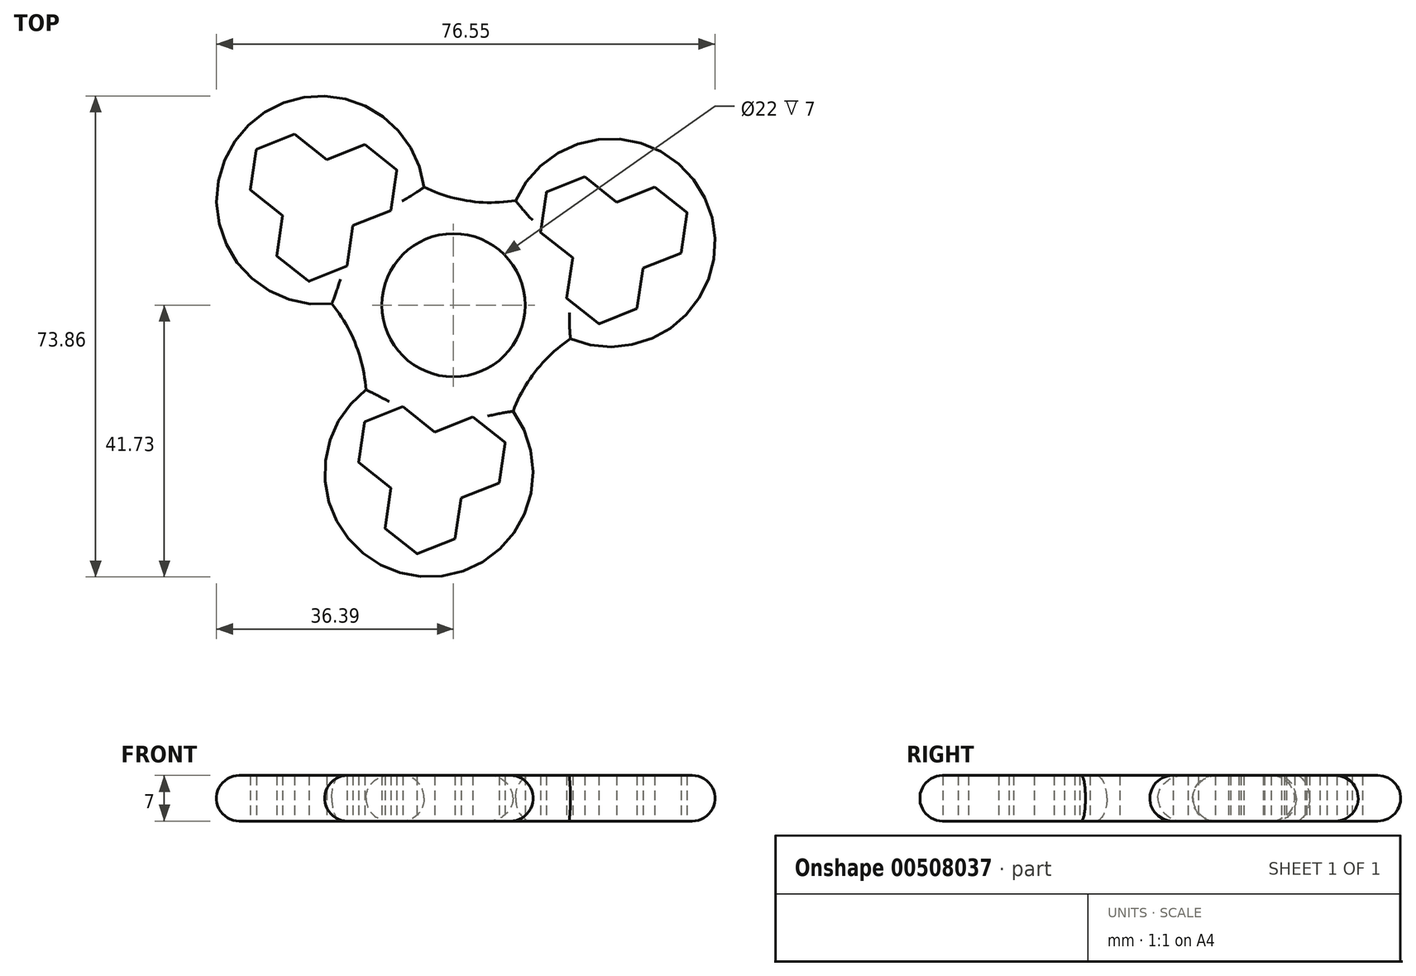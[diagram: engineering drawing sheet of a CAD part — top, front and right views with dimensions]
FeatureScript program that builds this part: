
annotation { "Feature Type Name" : "Feature", "Feature Type Description" : "" }
export const myFeature = defineFeature(function(context is Context, id is Id, definition is map)
    precondition{}
    {
        {
            var Q0;
            Q0=qCreatedBy(makeId("Top.planeOp"),FACE);
            var sketch = newSketch(context, id + "F0", { "sketchPlane" : qUnion([Q0])});
            skCircle(sketch, "E0", {"center": v(0, 0) * mm, "radius": 15 * mm});
            skCircle(sketch, "E1", {"center": v(0, 0) * mm, "radius": 11 * mm});
            skLineSegment(sketch, "E2", {"start": v(0, 0) * mm, "end": v(-20.4, 16.13) * mm});
            skLineSegment(sketch, "E3", {"start": v(0, 0) * mm, "end": v(24.16, 9.6) * mm});
            skLineSegment(sketch, "E4", {"start": v(0, 0) * mm, "end": v(-3.77, -25.73) * mm});
            skPoint(sketch, "E5.0.midPoint", {"position": v(-16.08, 12.72) * mm});
            skPoint(sketch, "E6.0.midPoint", {"position": v(19.05, 7.57) * mm});
            skPoint(sketch, "E7.0.midPoint", {"position": v(-2.97, -20.28) * mm});
            skCircle(sketch, "E8", {"center": v(-3.77, -25.73) * mm, "radius": 16 * mm});
            skCircle(sketch, "E9", {"center": v(-20.4, 16.13) * mm, "radius": 16 * mm});
            skCircle(sketch, "E10", {"center": v(24.16, 9.6) * mm, "radius": 16 * mm});
            skCircle(sketch, "E11.cCircle", {"center": v(-25.33, 20.03) * mm, "radius": 6.3 * mm, "construction": true});
            skLineSegment(sketch, "E11.0", {"start": v(-19.48, 22.35) * mm, "end": v(-20.4, 16.13) * mm});
            skLineSegment(sketch, "E11.1", {"start": v(-20.4, 16.13) * mm, "end": v(-26.24, 13.8) * mm});
            skLineSegment(sketch, "E11.2", {"start": v(-26.24, 13.8) * mm, "end": v(-31.18, 17.7) * mm});
            skLineSegment(sketch, "E11.3", {"start": v(-31.18, 17.7) * mm, "end": v(-30.27, 23.93) * mm});
            skLineSegment(sketch, "E11.4", {"start": v(-30.27, 23.93) * mm, "end": v(-24.42, 26.26) * mm});
            skLineSegment(sketch, "E11.5", {"start": v(-24.42, 26.26) * mm, "end": v(-19.48, 22.35) * mm});
            skCircle(sketch, "E12.cCircle", {"center": v(-14.55, 18.45) * mm, "radius": 6.3 * mm, "construction": true});
            skLineSegment(sketch, "E12.0", {"start": v(-8.7, 20.77) * mm, "end": v(-9.6, 14.55) * mm});
            skLineSegment(sketch, "E12.1", {"start": v(-9.6, 14.55) * mm, "end": v(-15.46, 12.22) * mm});
            skLineSegment(sketch, "E12.2", {"start": v(-15.46, 12.22) * mm, "end": v(-20.4, 16.13) * mm});
            skLineSegment(sketch, "E12.3", {"start": v(-20.4, 16.13) * mm, "end": v(-19.48, 22.35) * mm});
            skLineSegment(sketch, "E12.4", {"start": v(-19.48, 22.35) * mm, "end": v(-13.63, 24.68) * mm});
            skLineSegment(sketch, "E12.5", {"start": v(-13.63, 24.68) * mm, "end": v(-8.7, 20.77) * mm});
            skCircle(sketch, "E13.cCircle", {"center": v(-21.3, 9.9) * mm, "radius": 6.3 * mm, "construction": true});
            skLineSegment(sketch, "E13.0", {"start": v(-16.37, 6) * mm, "end": v(-22.22, 3.67) * mm});
            skLineSegment(sketch, "E13.1", {"start": v(-22.22, 3.67) * mm, "end": v(-27.16, 7.58) * mm});
            skLineSegment(sketch, "E13.2", {"start": v(-27.16, 7.58) * mm, "end": v(-26.24, 13.8) * mm});
            skLineSegment(sketch, "E13.3", {"start": v(-26.24, 13.8) * mm, "end": v(-20.4, 16.13) * mm});
            skLineSegment(sketch, "E13.4", {"start": v(-20.4, 16.13) * mm, "end": v(-15.46, 12.22) * mm});
            skLineSegment(sketch, "E13.5", {"start": v(-15.46, 12.22) * mm, "end": v(-16.37, 6) * mm});
            skCircle(sketch, "E14.MirrorC", {"center": v(30.01, 11.92) * mm, "radius": 6.3 * mm, "construction": true});
            skCircle(sketch, "E15.MirrorC", {"center": v(19.23, 13.5) * mm, "radius": 6.3 * mm, "construction": true});
            skCircle(sketch, "E16.MirrorC", {"center": v(23.25, 3.37) * mm, "radius": 6.3 * mm, "construction": true});
            skLineSegment(sketch, "E17.MirrorCS", {"start": v(30.92, 18.15) * mm, "end": v(25.08, 15.82) * mm});
            skLineSegment(sketch, "E18.MirrorCS", {"start": v(35.86, 14.24) * mm, "end": v(30.92, 18.15) * mm});
            skLineSegment(sketch, "E19.MirrorCS", {"start": v(34.95, 8.02) * mm, "end": v(35.86, 14.24) * mm});
            skLineSegment(sketch, "E20.MirrorCS", {"start": v(29.1, 5.7) * mm, "end": v(34.95, 8.02) * mm});
            skLineSegment(sketch, "E21.MirrorCS", {"start": v(24.16, 9.6) * mm, "end": v(29.1, 5.7) * mm});
            skLineSegment(sketch, "E22.MirrorCS", {"start": v(25.08, 15.82) * mm, "end": v(24.16, 9.6) * mm});
            skLineSegment(sketch, "E23.MirrorCS", {"start": v(25.08, 15.82) * mm, "end": v(20.14, 19.73) * mm});
            skLineSegment(sketch, "E24.MirrorCS", {"start": v(20.14, 19.73) * mm, "end": v(14.3, 17.4) * mm});
            skLineSegment(sketch, "E25.MirrorCS", {"start": v(14.3, 17.4) * mm, "end": v(13.38, 11.18) * mm});
            skLineSegment(sketch, "E26.MirrorCS", {"start": v(13.38, 11.18) * mm, "end": v(18.31, 7.28) * mm});
            skLineSegment(sketch, "E27.MirrorCS", {"start": v(18.31, 7.28) * mm, "end": v(24.16, 9.6) * mm});
            skLineSegment(sketch, "E28.MirrorCS", {"start": v(28.19, -0.53) * mm, "end": v(29.1, 5.7) * mm});
            skLineSegment(sketch, "E29.MirrorCS", {"start": v(22.34, -2.85) * mm, "end": v(28.19, -0.53) * mm});
            skLineSegment(sketch, "E30.MirrorCS", {"start": v(17.4, 1.05) * mm, "end": v(22.34, -2.85) * mm});
            skLineSegment(sketch, "E31.MirrorCS", {"start": v(18.31, 7.28) * mm, "end": v(17.4, 1.05) * mm});
            skLineSegment(sketch, "E32.MirrorCS", {"start": v(-14.55, -24.15) * mm, "end": v(-13.64, -17.92) * mm});
            skLineSegment(sketch, "E33.MirrorCS", {"start": v(-9.62, -28.05) * mm, "end": v(-14.55, -24.15) * mm});
            skLineSegment(sketch, "E34.MirrorCS", {"start": v(-13.64, -17.92) * mm, "end": v(-7.8, -15.6) * mm});
            skLineSegment(sketch, "E35.MirrorCS", {"start": v(-9.62, -28.05) * mm, "end": v(-3.77, -25.73) * mm});
            skLineSegment(sketch, "E36.MirrorCS", {"start": v(-10.53, -34.28) * mm, "end": v(-9.62, -28.05) * mm});
            skLineSegment(sketch, "E37.MirrorCS", {"start": v(-5.6, -38.18) * mm, "end": v(-10.53, -34.28) * mm});
            skLineSegment(sketch, "E38.MirrorCS", {"start": v(0.25, -35.86) * mm, "end": v(-5.6, -38.18) * mm});
            skLineSegment(sketch, "E39.MirrorCS", {"start": v(1.17, -29.63) * mm, "end": v(0.25, -35.86) * mm});
            skLineSegment(sketch, "E40.MirrorCS", {"start": v(-3.77, -25.73) * mm, "end": v(1.17, -29.63) * mm});
            skLineSegment(sketch, "E41.MirrorCS", {"start": v(-2.86, -19.5) * mm, "end": v(3, -17.18) * mm});
            skLineSegment(sketch, "E42.MirrorCS", {"start": v(7.02, -27.3) * mm, "end": v(1.17, -29.63) * mm});
            skLineSegment(sketch, "E43.MirrorCS", {"start": v(7.93, -21.08) * mm, "end": v(7.02, -27.3) * mm});
            skLineSegment(sketch, "E44.MirrorCS", {"start": v(3, -17.18) * mm, "end": v(7.93, -21.08) * mm});
            skLineSegment(sketch, "E45.MirrorCS", {"start": v(-7.8, -15.6) * mm, "end": v(-2.86, -19.5) * mm});
            skCircle(sketch, "E46.MirrorC", {"center": v(-8.7, -21.82) * mm, "radius": 6.3 * mm, "construction": true});
            skCircle(sketch, "E47.MirrorC", {"center": v(-4.68, -31.95) * mm, "radius": 6.3 * mm, "construction": true});
            skCircle(sketch, "E48.MirrorC", {"center": v(2.08, -23.4) * mm, "radius": 6.3 * mm, "construction": true});
            skLineSegment(sketch, "E49", {"start": v(-8.7, 20.77) * mm, "end": v(14.3, 17.4) * mm, "construction": true});
            skLineSegment(sketch, "E50", {"start": v(22.34, -2.85) * mm, "end": v(7.93, -21.08) * mm, "construction": true});
            skLineSegment(sketch, "E51", {"start": v(-13.64, -17.92) * mm, "end": v(-22.22, 3.67) * mm, "construction": true});
            skArc(sketch, "E52", {"start": v(-8.7, 20.77) * mm, "mid": v(2.35, 16) * mm, "end": v(14.3, 17.4) * mm});
            skArc(sketch, "E53", {"start": v(22.34, -2.85) * mm, "mid": v(12.7, -10.04) * mm, "end": v(7.93, -21.08) * mm});
            skArc(sketch, "E54", {"start": v(-13.64, -17.92) * mm, "mid": v(-15.04, -5.97) * mm, "end": v(-22.22, 3.67) * mm});
            skSolve(sketch);
        }
        {
            var Q0;
            Q0=qSketchRegion(id+"F0",true);
            var Q1;
            {var subQ5=sQuery(id+"F0.wireOp",EDGE,"E10");var subQ6=sQuery(id+"F0.wireOp",EDGE,"E0");var subQ7=makeQuery(id+"F0.imprint","INTERSECT",VERTEX,{"disambiguationData":[OD(1.0)],"derivedFrom":[subQ6,subQ5]});Q1=makeQuery(id+"F0.imprint","IMPRINT",FACE,{"disambiguationData":[TD([[makeQuery(id+"F0.imprint","IMPRINT",EDGE,{"disambiguationData":[TD([[subQ7,-1.0]])],"derivedFrom":subQ6}),1.0]])]});}
            var Q2;
            {var subQ3=sQuery(id+"F0.wireOp",EDGE,"E10");var subQ6=sQuery(id+"F0.wireOp",EDGE,"E0");var subQ10=makeQuery(id+"F0.imprint","INTERSECT",VERTEX,{"disambiguationData":[OD(0.0)],"derivedFrom":[subQ6,subQ3]});Q2=makeQuery(id+"F0.imprint","IMPRINT",FACE,{"disambiguationData":[TD([[makeQuery(id+"F0.imprint","IMPRINT",EDGE,{"disambiguationData":[TD([[subQ10,1.0]])],"derivedFrom":subQ6}),1.0]])]});}
            var Q3;
            {var subQ1=sQuery(id+"F0.wireOp",EDGE,"E0");var subQ8=sQuery(id+"F0.wireOp",EDGE,"E9");var subQ11=makeQuery(id+"F0.imprint","INTERSECT",VERTEX,{"disambiguationData":[OD(1.0)],"derivedFrom":[subQ1,subQ8]});Q3=makeQuery(id+"F0.imprint","IMPRINT",FACE,{"disambiguationData":[TD([[makeQuery(id+"F0.imprint","IMPRINT",EDGE,{"disambiguationData":[TD([[subQ11,-1.0]])],"derivedFrom":subQ1}),1.0]])]});}
            var Q4;
            {var subQ0=sQuery(id+"F0.wireOp",EDGE,"E2");var subQ1=sQuery(id+"F0.wireOp",EDGE,"E0");var subQ2=makeQuery(id+"F0.imprint","INTERSECT",VERTEX,{"derivedFrom":[subQ1,subQ0]});Q4=makeQuery(id+"F0.imprint","IMPRINT",FACE,{"disambiguationData":[TD([[makeQuery(id+"F0.imprint","IMPRINT",EDGE,{"disambiguationData":[TD([[subQ2,-1.0]])],"derivedFrom":subQ1}),1.0]])]});}
            var Q5;
            {var subQ0=sQuery(id+"F0.wireOp",EDGE,"E9");var subQ1=sQuery(id+"F0.wireOp",EDGE,"E0");var subQ2=makeQuery(id+"F0.imprint","INTERSECT",VERTEX,{"disambiguationData":[OD(0.0)],"derivedFrom":[subQ1,subQ0]});Q5=makeQuery(id+"F0.imprint","IMPRINT",FACE,{"disambiguationData":[TD([[makeQuery(id+"F0.imprint","IMPRINT",EDGE,{"disambiguationData":[TD([[subQ2,-1.0]])],"derivedFrom":subQ1}),1.0]])]});}
            var Q6;
            {var subQ0=sQuery(id+"F0.wireOp",EDGE,"E3");var subQ1=sQuery(id+"F0.wireOp",EDGE,"E0");var subQ2=makeQuery(id+"F0.imprint","INTERSECT",VERTEX,{"derivedFrom":[subQ1,subQ0]});Q6=makeQuery(id+"F0.imprint","IMPRINT",FACE,{"disambiguationData":[TD([[makeQuery(id+"F0.imprint","IMPRINT",EDGE,{"disambiguationData":[TD([[subQ2,-1.0]])],"derivedFrom":subQ1}),1.0]])]});}
            var Q7;
            {var subQ0=sQuery(id+"F0.wireOp",EDGE,"E3");var subQ1=sQuery(id+"F0.wireOp",EDGE,"E0");var subQ2=makeQuery(id+"F0.imprint","INTERSECT",VERTEX,{"derivedFrom":[subQ1,subQ0]});Q7=makeQuery(id+"F0.imprint","IMPRINT",FACE,{"disambiguationData":[TD([[makeQuery(id+"F0.imprint","IMPRINT",EDGE,{"disambiguationData":[TD([[subQ2,1.0]])],"derivedFrom":subQ1}),1.0]])]});}
            var Q8;
            {var subQ0=sQuery(id+"F0.wireOp",EDGE,"E8");var subQ1=sQuery(id+"F0.wireOp",EDGE,"E0");var subQ2=makeQuery(id+"F0.imprint","INTERSECT",VERTEX,{"disambiguationData":[OD(0.0)],"derivedFrom":[subQ1,subQ0]});Q8=makeQuery(id+"F0.imprint","IMPRINT",FACE,{"disambiguationData":[TD([[makeQuery(id+"F0.imprint","IMPRINT",EDGE,{"disambiguationData":[TD([[subQ2,-1.0]])],"derivedFrom":subQ1}),1.0]])]});}
            var Q9;
            {var subQ0=sQuery(id+"F0.wireOp",EDGE,"E4");var subQ1=sQuery(id+"F0.wireOp",EDGE,"E0");var subQ2=makeQuery(id+"F0.imprint","INTERSECT",VERTEX,{"derivedFrom":[subQ1,subQ0]});Q9=makeQuery(id+"F0.imprint","IMPRINT",FACE,{"disambiguationData":[TD([[makeQuery(id+"F0.imprint","IMPRINT",EDGE,{"disambiguationData":[TD([[subQ2,-1.0]])],"derivedFrom":subQ1}),1.0]])]});}
            var Q10;
            {var subQ3=sQuery(id+"F0.wireOp",EDGE,"E10");var subQ6=sQuery(id+"F0.wireOp",EDGE,"E0");var subQ11=makeQuery(id+"F0.imprint","INTERSECT",VERTEX,{"disambiguationData":[OD(0.0)],"derivedFrom":[subQ6,subQ3]});Q10=makeQuery(id+"F0.imprint","IMPRINT",FACE,{"disambiguationData":[TD([[makeQuery(id+"F0.imprint","IMPRINT",EDGE,{"disambiguationData":[TD([[subQ11,-1.0]])],"derivedFrom":subQ6}),1.0]])]});}
            var Q11;
            {var subQ0=sQuery(id+"F0.wireOp",EDGE,"E8");var subQ1=sQuery(id+"F0.wireOp",EDGE,"E0");var subQ2=makeQuery(id+"F0.imprint","INTERSECT",VERTEX,{"disambiguationData":[OD(1.0)],"derivedFrom":[subQ1,subQ0]});Q11=makeQuery(id+"F0.imprint","IMPRINT",FACE,{"disambiguationData":[TD([[makeQuery(id+"F0.imprint","IMPRINT",EDGE,{"disambiguationData":[TD([[subQ2,-1.0]])],"derivedFrom":subQ1}),1.0]])]});}
            extrude(context, id + "F1", {"entities" : qUnion([Q0, Q1, Q2, Q3, Q4, Q5, Q6, Q7, Q8, Q9, Q10, Q11]), "depth" : 7 * mm});
        }
        {
            var Q0;
            Q0=makeQuery(id+"F1.opExtrude","CAP_EDGE",EDGE,{"disambiguationData":[OSD([sQuery(id+"F0.wireOp",EDGE,"E9")])],"isStart":false});
            var Q1;
            Q1=makeQuery(id+"F1.opExtrude","CAP_EDGE",EDGE,{"disambiguationData":[OSD([sQuery(id+"F0.wireOp",EDGE,"E9")])],"isStart":true});
            var Q2;
            Q2=makeQuery(id+"F1.opExtrude","CAP_EDGE",EDGE,{"disambiguationData":[OSD([sQuery(id+"F0.wireOp",EDGE,"E54")])],"isStart":false});
            var Q3;
            Q3=makeQuery(id+"F1.opExtrude","CAP_EDGE",EDGE,{"disambiguationData":[OSD([sQuery(id+"F0.wireOp",EDGE,"E52")])],"isStart":false});
            var Q4;
            Q4=makeQuery(id+"F1.opExtrude","CAP_EDGE",EDGE,{"disambiguationData":[OSD([sQuery(id+"F0.wireOp",EDGE,"E54")])],"isStart":true});
            var Q5;
            Q5=makeQuery(id+"F1.opExtrude","CAP_EDGE",EDGE,{"disambiguationData":[OSD([sQuery(id+"F0.wireOp",EDGE,"E52")])],"isStart":true});
            var Q6;
            Q6=makeQuery(id+"F1.opExtrude","CAP_EDGE",EDGE,{"disambiguationData":[OSD([sQuery(id+"F0.wireOp",EDGE,"E10")])],"isStart":true});
            var Q7;
            Q7=makeQuery(id+"F1.opExtrude","CAP_EDGE",EDGE,{"disambiguationData":[OSD([sQuery(id+"F0.wireOp",EDGE,"E10")])],"isStart":false});
            var Q8;
            Q8=makeQuery(id+"F1.opExtrude","CAP_EDGE",EDGE,{"disambiguationData":[OSD([sQuery(id+"F0.wireOp",EDGE,"E53")])],"isStart":false});
            var Q9;
            Q9=makeQuery(id+"F1.opExtrude","CAP_EDGE",EDGE,{"disambiguationData":[OSD([sQuery(id+"F0.wireOp",EDGE,"E53")])],"isStart":true});
            var Q10;
            Q10=makeQuery(id+"F1.opExtrude","CAP_EDGE",EDGE,{"disambiguationData":[OSD([sQuery(id+"F0.wireOp",EDGE,"E8")])],"isStart":false});
            var Q11;
            Q11=makeQuery(id+"F1.opExtrude","CAP_EDGE",EDGE,{"disambiguationData":[OSD([sQuery(id+"F0.wireOp",EDGE,"E8")])],"isStart":true});
            fillet(context, id + "F2", {"entities" : qUnion([Q0, Q1, Q2, Q3, Q4, Q5, Q6, Q7, Q8, Q9, Q10, Q11]), "radius" : 3.5 * mm, "tangentPropagation" : true, "allowEdgeOverflow" : false});
        }
    });
